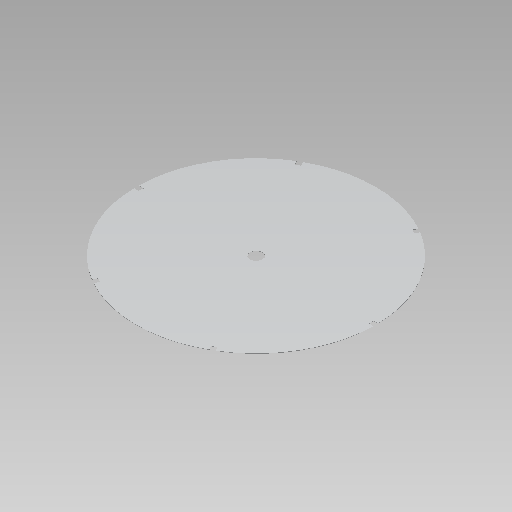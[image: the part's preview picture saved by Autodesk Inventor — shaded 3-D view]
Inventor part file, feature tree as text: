
AUTODESK INVENTOR PART (.ipt)
format: ipt  version: 2017 (Build 210142000, 142)  size: 144,384 bytes
history: native  units: in
note: dims shown in document units (in); Inventor stores cm internally (conversion verified against a paired STEP export)
features: extrude x3, sketch x3, pattern_circular x1
ambient origin geometry x8: Origin, YZ Plane, XZ Plane, XY Plane, X Axis, Y Axis, Z Axis, Center Point
bodies: Solid1 (feature_tree)
feature tree (7):
  extrude  "Extrusion1"  Depth=0.1in TaperAngle=0.0deg
  extrude  "Extrusion2"  Depth=1.0in TaperAngle=0.0deg
  extrude  "Extrusion3"  Depth=0.3937in TaperAngle=360.0deg
  pattern_circular  "Circular Pattern1"  [2 undecoded]
  sketch  "Sketch1"  dims[d0=67.7165in d1=0.1in d2=0.0in]
  sketch  "Sketch2"  dims[d7=3.5433in d9=1.0in d10=0.0in]
  sketch  "Sketch3"  dims[d14=0.3937in d15=0.0in d16=2.3622in d17=360.0deg]
note: 2 required parameter values undecoded (feature->parameter linkage not recoverable at this tier; creation-order binding heuristic only, values carry confidence <= 0.55)
